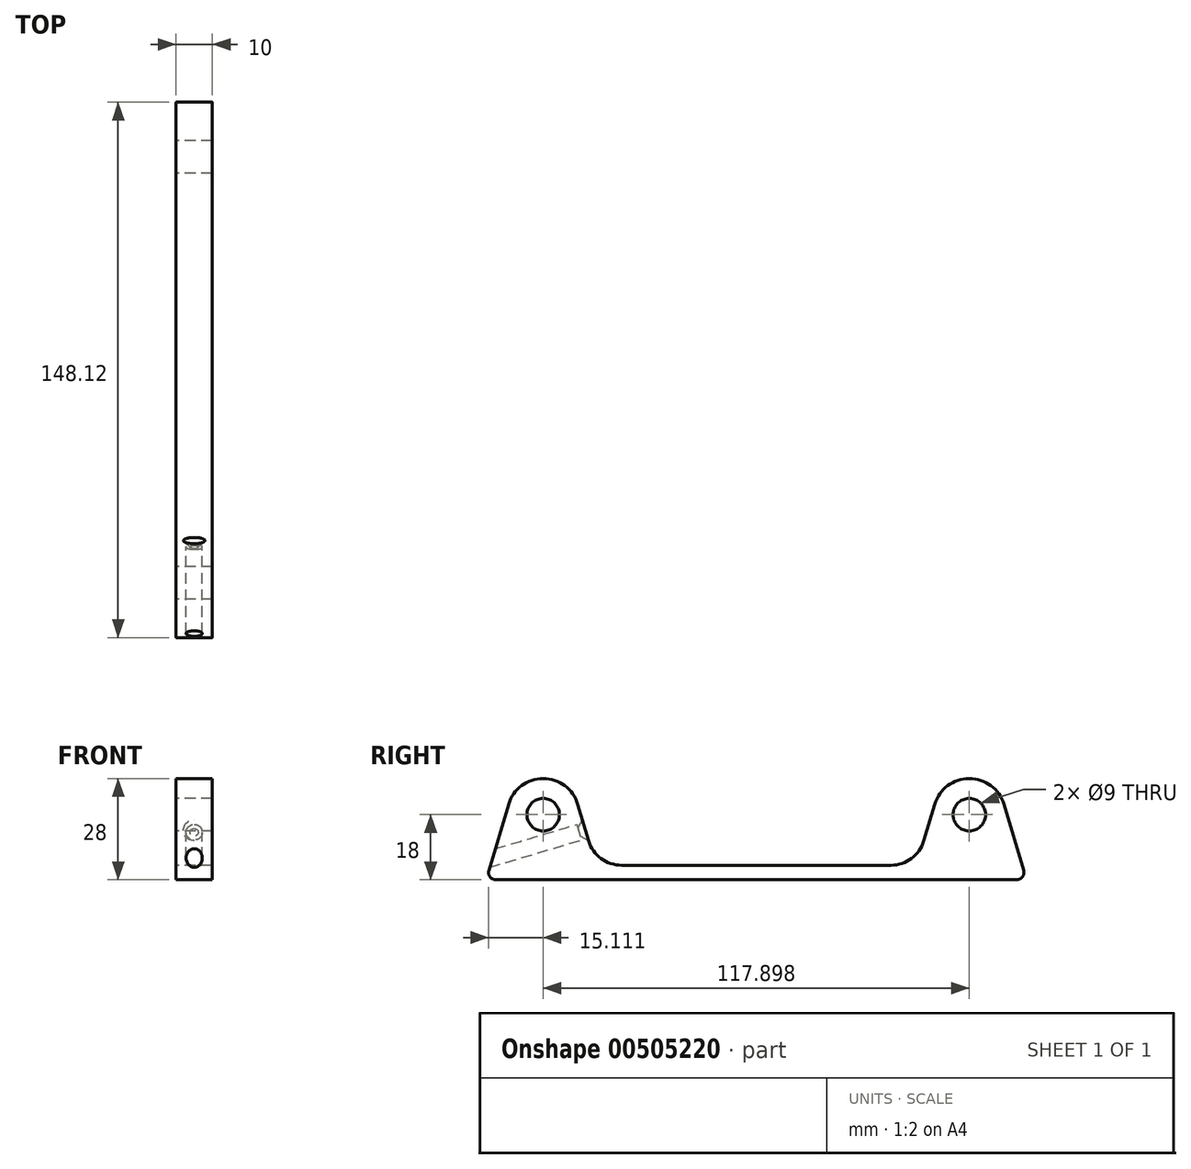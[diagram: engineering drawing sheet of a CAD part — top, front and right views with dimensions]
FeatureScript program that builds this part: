
annotation { "Feature Type Name" : "Feature", "Feature Type Description" : "" }
export const myFeature = defineFeature(function(context is Context, id is Id, definition is map)
    precondition{}
    {
        {
            var Q0;
            Q0=qCreatedBy(makeId("Right.planeOp"),FACE);
            var sketch = newSketch(context, id + "F0", { "sketchPlane" : qUnion([Q0])});
            skCircle(sketch, "E0", {"center": v(-58.95, 18) * mm, "radius": 16 * mm, "construction": true});
            skCircle(sketch, "E1", {"center": v(-58.95, 18) * mm, "radius": 12 * mm, "construction": true});
            skCircle(sketch, "E2", {"center": v(0, 75) * mm, "radius": 70 * mm, "construction": true});
            skCircle(sketch, "E3.MirrorC", {"center": v(58.95, 18) * mm, "radius": 12 * mm, "construction": true});
            skCircle(sketch, "E4.MirrorC", {"center": v(58.95, 18) * mm, "radius": 16 * mm, "construction": true});
            skCircle(sketch, "E5", {"center": v(0, 113.23) * mm, "radius": 100 * mm, "construction": true});
            skSolve(sketch);
        }
        {
            var Q0;
            Q0=qCreatedBy(makeId("Right.planeOp"),FACE);
            var sketch = newSketch(context, id + "F1", { "sketchPlane" : qUnion([Q0])});
            skCircle(sketch, "E6", {"center": v(-58.95, 18) * mm, "radius": 4.5 * mm});
            skCircle(sketch, "E7", {"center": v(58.95, 18) * mm, "radius": 4.5 * mm});
            skArc(sketch, "E8", {"start": v(-68.53, 20.85) * mm, "mid": v(-58.95, 28) * mm, "end": v(-49.36, 20.85) * mm});
            skLineSegment(sketch, "E9", {"start": v(-49.36, 20.85) * mm, "end": v(-46.37, 10.79) * mm});
            skLineSegment(sketch, "E10", {"start": v(-68.53, 20.85) * mm, "end": v(-73.98, 2.57) * mm});
            skArc(sketch, "E11", {"start": v(-46.37, 10.79) * mm, "mid": v(-42.94, 5.88) * mm, "end": v(-37.26, 4) * mm});
            skLineSegment(sketch, "E12", {"start": v(-37.26, 4) * mm, "end": v(0, 4) * mm});
            skArc(sketch, "E13", {"start": v(-73.98, 2.57) * mm, "mid": v(-73.66, 0.8) * mm, "end": v(-72.06, 0) * mm});
            skLineSegment(sketch, "E14", {"start": v(-72.06, 0) * mm, "end": v(0, 0) * mm});
            skLineSegment(sketch, "E15", {"start": v(-47.22, 13.67) * mm, "end": v(-72.95, 6) * mm, "construction": true});
            skLineSegment(sketch, "E16", {"start": v(-46.37, 10.79) * mm, "end": v(-73.98, 2.57) * mm, "construction": true});
            skLineSegment(sketch, "E17.MirrorCS", {"start": v(72.06, 0) * mm, "end": v(0, 0) * mm});
            skArc(sketch, "E18.MirrorCS", {"start": v(73.98, 2.57) * mm, "mid": v(73.66, 0.8) * mm, "end": v(72.06, 0) * mm});
            skLineSegment(sketch, "E19.MirrorCS", {"start": v(68.53, 20.85) * mm, "end": v(73.98, 2.57) * mm});
            skArc(sketch, "E20.MirrorCS", {"start": v(68.53, 20.85) * mm, "mid": v(58.95, 28) * mm, "end": v(49.36, 20.85) * mm});
            skLineSegment(sketch, "E21.MirrorCS", {"start": v(49.36, 20.85) * mm, "end": v(46.37, 10.79) * mm});
            skArc(sketch, "E22.MirrorCS", {"start": v(46.37, 10.79) * mm, "mid": v(42.94, 5.88) * mm, "end": v(37.26, 4) * mm});
            skLineSegment(sketch, "E23.MirrorCS", {"start": v(37.26, 4) * mm, "end": v(0, 4) * mm});
            skSolve(sketch);
        }
        {
            var Q0;
            Q0=makeQuery(id+"F1.imprint","IMPRINT",FACE,{"disambiguationData":[TD([[makeQuery(id+"F1.imprint","IMPRINT",EDGE,{"derivedFrom":sQuery(id+"F1.wireOp",EDGE,"E6")}),-1.0]])]});
            extrude(context, id + "F2", {"entities" : qUnion([Q0]), "endBound" : BoundingType.SYMMETRIC, "depth" : 10 * mm, "offsetDistance" : 25 * mm});
        }
        {
            var Q0;
            Q0=qCreatedBy(makeId("Right.planeOp"),FACE);
            var sketch = newSketch(context, id + "F3", { "sketchPlane" : qUnion([Q0])});
            skLineSegment(sketch, "E24", {"start": v(-48.38, 10.97) * mm, "end": v(-74.2, 3.29) * mm});
            skLineSegment(sketch, "E25", {"start": v(-74.2, 3.29) * mm, "end": v(-73.98, 2.57) * mm, "construction": true});
            skLineSegment(sketch, "E26", {"start": v(-48.38, 10.97) * mm, "end": v(-48.7, 12.05) * mm});
            skLineSegment(sketch, "E27", {"start": v(-48.7, 12.05) * mm, "end": v(-46.37, 10.79) * mm});
            skLineSegment(sketch, "E28.MirrorCS", {"start": v(-49.66, 15.29) * mm, "end": v(-75.47, 7.6) * mm});
            skLineSegment(sketch, "E29.MirrorCS", {"start": v(-49.66, 15.29) * mm, "end": v(-49.34, 14.2) * mm});
            skLineSegment(sketch, "E30.MirrorCS", {"start": v(-49.34, 14.2) * mm, "end": v(-48.08, 16.54) * mm});
            skLineSegment(sketch, "E31", {"start": v(-75.47, 7.6) * mm, "end": v(-74.2, 3.29) * mm});
            skLineSegment(sketch, "E32", {"start": v(-48.08, 16.54) * mm, "end": v(-46.37, 10.79) * mm});
            skLineSegment(sketch, "E33", {"start": v(-49.34, 14.2) * mm, "end": v(-48.7, 12.05) * mm, "construction": true});
            skLineSegment(sketch, "E34", {"start": v(-74.83, 5.45) * mm, "end": v(-47.22, 13.67) * mm});
            skSolve(sketch);
        }
        {
            var Q0;
            {var subQ1=sQuery(id+"F3.wireOp",EDGE,"E24");Q0=makeQuery(id+"F3.imprint","IMPRINT",FACE,{"disambiguationData":[TD([[makeQuery(id+"F3.imprint","IMPRINT",EDGE,{"derivedFrom":subQ1}),-1.0]])]});}
            var Q1;
            Q1=sQuery(id+"F3.wireOp",EDGE,"E34");
            revolve(context, id + "F4", {"operationType" : NewBodyOperationType.REMOVE, "surfaceOperationType" : NewSurfaceOperationType.NEW, "entities" : qUnion([Q0]), "axis" : qUnion([Q1]), "revolveType" : RevolveType.FULL, "oppositeDirection" : true});
        }
    });
